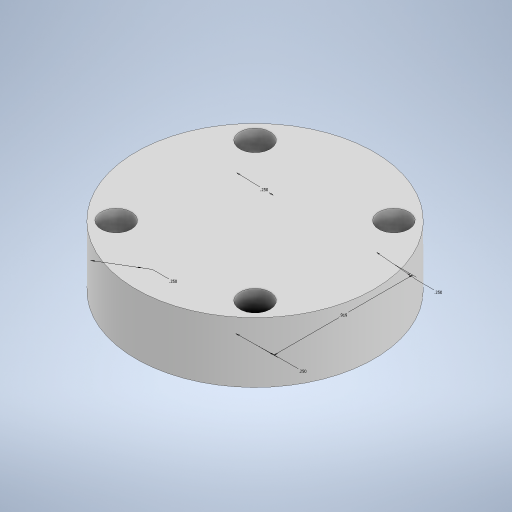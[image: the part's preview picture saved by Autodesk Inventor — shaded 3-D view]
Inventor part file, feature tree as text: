
AUTODESK INVENTOR PART (.ipt)
format: ipt  version: 2023 (Build 270158000, 158)  size: 266,752 bytes
history: native  units: in
note: dims shown in document units (in); Inventor stores cm internally (conversion verified against a paired STEP export)
features: sketch x5, extrude x4
ambient origin geometry x8: Origin, YZ Plane, XZ Plane, XY Plane, X Axis, Y Axis, Z Axis, Center Point
bodies: Solid1 (feature_tree)
feature tree (9):
  extrude  "Extrusion1"  Depth=0.919in
  extrude  "Extrusion2"  Depth=0.098in
  sketch  "Sketch5"  dims[d4=0.098in d5=0.098in]
  sketch  "Sketch6"  dims[d6=0.098in d7=0.15in d8=0.0in]
  extrude  "Extrusion3"  Depth=0.098in
  extrude  "Extrusion4"  Depth=0.15in TaperAngle=0.0deg
  sketch  "Sketch1"  dims[d0=1.575in d1=0.919in]
  sketch  "Sketch3"  dims[d2=0.919in d3=0.098in]
  sketch  "Sketch7"  dims[d10=0.125in d11=0.25in d12=0.0in d13=0.919in d14=0.25in d15=0.25in d16=0.25in d17=0.25in d18=0.25in d19=0.0in d20=0.919in d21=0.919in d22=0.2in d23=0.2in d24=0.2in d25=0.2in d26=0.25in d27=0.0in]
